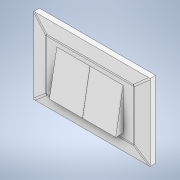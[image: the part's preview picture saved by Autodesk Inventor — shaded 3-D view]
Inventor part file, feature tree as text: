
AUTODESK INVENTOR PART (.ipt)
format: ipt  version: 2022 (Build 260153000, 153)  size: 164,352 bytes
history: native  units: mm
features: sketch x4, chamfer x4, other x3, extrude x3, fillet x1, projected_geometry x1
ambient origin geometry x8: Origin, YZ Plane, XZ Plane, XY Plane, X Axis, Y Axis, Z Axis, Center Point
bodies: Body1 (feature_tree)
feature tree (16):
  other  "솔리드1"
  extrude  "돌출1"  Depth=80.0mm
  sketch  "스케치2"
  other  "작업 평면1"
  extrude  "돌출2"  Depth=122.0mm
  other  "작업 평면2"
  extrude  "돌출3"  Depth=7.8mm TaperAngle=0.0deg
  chamfer  "모따기1"  Distance=43.5mm
  chamfer  "모따기2"  Distance=69.5mm
  chamfer  "모따기3"  Distance=26.25mm
  chamfer  "모따기4"  Distance=18.25mm
  fillet  "모깎기1"  [1 undecoded]
  sketch  "스케치1"
  sketch  "스케치3"
  sketch  "스케치4"
  projected_geometry  "투영된 루프1"
note: 1 required parameter value undecoded (feature->parameter linkage not recoverable at this tier; creation-order binding heuristic only, values carry confidence <= 0.55)
